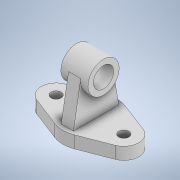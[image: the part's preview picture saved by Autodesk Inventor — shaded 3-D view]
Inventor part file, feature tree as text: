
AUTODESK INVENTOR PART (.ipt)
format: ipt  version: 2022.2 (Build 262287030, 287C)  size: 151,040 bytes
history: native  units: in
note: dims shown in document units (in); Inventor stores cm internally (conversion verified against a paired STEP export)
features: extrude x3, sketch x2, projected_geometry x1
ambient origin geometry x8: Origin, YZ Plane, XZ Plane, XY Plane, X Axis, Y Axis, Z Axis, Center Point
bodies: Solid1 (feature_tree)
feature tree (6):
  extrude  "Extrusion1"  Depth=1.5748in
  sketch  "Sketch2"  dims[d2=0.5906in d3=0.8661in d4=0.7087in d5=0.0in d7=2.6378in d8=1.811in d9=1.1811in d10=0.7087in d11=0.0in d12=1.5748in d13=0.0in d14=4.5669in]
  extrude  "Extrusion2"  Depth=0.8661in
  extrude  "Extrusion3"  Depth=0.7087in TaperAngle=0.0deg
  sketch  "Sketch1"  dims[d0=3.937in d1=1.5748in]
  projected_geometry  "Projected Loop1"
